# Revit family: Trap-Bottle-Caroma Modina
name_source: partatom
category: Pipe Fittings
revit_build: Autodesk Revit 2014 (Build: 20131024_2115(x64)
units: mm (PartAtom-declared; Revit-internal decimal feet)

## types (1)
- Standard
    Assembly Code = D2030300
    CW Connection = No
    Description = Caroma Modina Bottle Trap
    Diameter_ANZRS = 40 mm  [stored 0.131234 ft]
    HW Connection = No
    Height_ANZRS = 330 mm
    K Coefficient = 0
    Keynote = BT
    Length_ANZRS = 62 mm  [stored 0.203412 ft]
    Manufacturer = GWA Bathroom & Kitchens
    Material_ANZRS = Metal-Chrome-Caroma
    Model = 687290C
    Side1Flow_ANZRS = 0.0 L/s
    Type Comments = 40mm Connection
    URL = http://www.caroma.com.au
    Vent Connection = No
    Waste Connection = No

note: [stored X ft] marks values corroborated as IEEE doubles in the binary element streams (Revit-internal decimal feet)

## geometry (parser evidence)
native form markers: Blend x14, Sweep x1
no freeform markers — native parametric forms only
